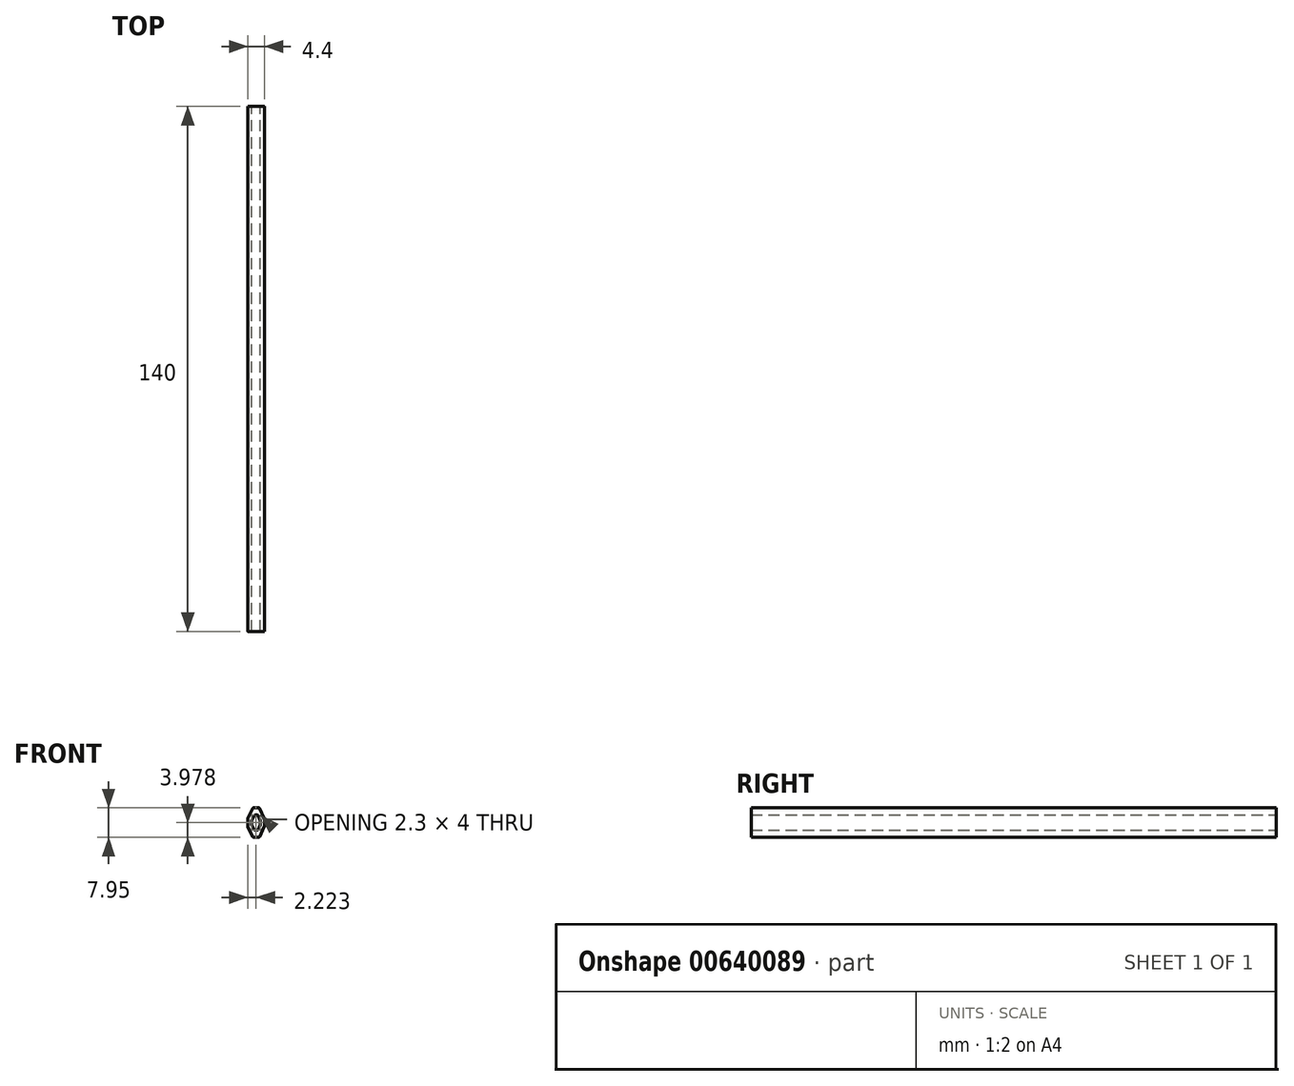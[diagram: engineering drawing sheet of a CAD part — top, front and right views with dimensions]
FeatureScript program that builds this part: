
annotation { "Feature Type Name" : "Feature", "Feature Type Description" : "" }
export const myFeature = defineFeature(function(context is Context, id is Id, definition is map)
    precondition{}
    {
        {
            var Q0;
            Q0=qCreatedBy(makeId("Front.planeOp"),FACE);
            var sketch = newSketch(context, id + "F0", { "sketchPlane" : qUnion([Q0])});
            skLineSegment(sketch, "E0", {"start": v(0, 5.06) * mm, "end": v(0, 2.96) * mm});
            skLineSegment(sketch, "E1", {"start": v(0, 2.96) * mm, "end": v(1.41, 0) * mm});
            skLineSegment(sketch, "E2", {"start": v(1.41, 0) * mm, "end": v(3.03, 0) * mm});
            skLineSegment(sketch, "E3", {"start": v(3.03, 0) * mm, "end": v(4.4, 2.87) * mm});
            skLineSegment(sketch, "E4", {"start": v(4.4, 2.87) * mm, "end": v(4.4, 5.06) * mm});
            skLineSegment(sketch, "E5", {"start": v(4.4, 5.06) * mm, "end": v(3.05, 7.95) * mm});
            skLineSegment(sketch, "E6", {"start": v(3.05, 7.95) * mm, "end": v(1.41, 7.95) * mm});
            skLineSegment(sketch, "E7", {"start": v(1.41, 7.95) * mm, "end": v(0, 5.06) * mm});
            skLineSegment(sketch, "E8", {"start": v(1.07, 4.51) * mm, "end": v(1.07, 3.41) * mm});
            skLineSegment(sketch, "E9", {"start": v(1.07, 3.41) * mm, "end": v(1.76, 1.98) * mm});
            skLineSegment(sketch, "E10", {"start": v(1.76, 1.98) * mm, "end": v(2.69, 1.98) * mm});
            skLineSegment(sketch, "E11", {"start": v(2.69, 1.98) * mm, "end": v(3.37, 3.41) * mm});
            skLineSegment(sketch, "E12", {"start": v(3.37, 3.41) * mm, "end": v(3.37, 4.51) * mm});
            skLineSegment(sketch, "E13", {"start": v(3.37, 4.51) * mm, "end": v(2.69, 5.98) * mm});
            skLineSegment(sketch, "E14", {"start": v(2.69, 5.98) * mm, "end": v(1.79, 5.98) * mm});
            skLineSegment(sketch, "E15", {"start": v(1.79, 5.98) * mm, "end": v(1.07, 4.51) * mm});
            skLineSegment(sketch, "E16", {"start": v(3.37, 4.51) * mm, "end": v(4.4, 5.06) * mm, "construction": true});
            skLineSegment(sketch, "E17", {"start": v(3.37, 3.41) * mm, "end": v(4.4, 2.87) * mm, "construction": true});
            skLineSegment(sketch, "E18", {"start": v(1.07, 3.41) * mm, "end": v(0, 2.96) * mm, "construction": true});
            skLineSegment(sketch, "E19", {"start": v(2.69, 1.98) * mm, "end": v(3.03, 0) * mm, "construction": true});
            skLineSegment(sketch, "E20", {"start": v(1.76, 1.98) * mm, "end": v(1.41, 0) * mm, "construction": true});
            skLineSegment(sketch, "E21", {"start": v(1.41, 7.95) * mm, "end": v(1.79, 5.98) * mm, "construction": true});
            skLineSegment(sketch, "E22", {"start": v(0, 5.06) * mm, "end": v(4.4, 5.06) * mm, "construction": true});
            skLineSegment(sketch, "E23", {"start": v(1.41, 0) * mm, "end": v(1.41, 7.95) * mm, "construction": true});
            skLineSegment(sketch, "E24", {"start": v(1.07, 3.41) * mm, "end": v(3.37, 3.41) * mm, "construction": true});
            skSolve(sketch);
        }
        {
            var Q0;
            Q0=makeQuery(id+"F0.imprint","IMPRINT",FACE,{"disambiguationData":[TD([[makeQuery(id+"F0.imprint","IMPRINT",EDGE,{"derivedFrom":sQuery(id+"F0.wireOp",EDGE,"E0")}),1.0]])]});
            extrude(context, id + "F1", {"entities" : qUnion([Q0]), "depth" : 140 * mm, "offsetDistance" : 25 * mm});
        }
        {
            var Q0;
            Q0=makeQuery(id+"F1.opExtrude","SWEPT_EDGE",EDGE,{"disambiguationData":[OSD([sQuery(id+"F0.wireOp",EDGE,"E5"),sQuery(id+"F0.wireOp",EDGE,"E6")])]});
            var Q1;
            Q1=makeQuery(id+"F1.opExtrude","SWEPT_EDGE",EDGE,{"disambiguationData":[OSD([sQuery(id+"F0.wireOp",EDGE,"E6"),sQuery(id+"F0.wireOp",EDGE,"E7")])]});
            var Q2;
            Q2=makeQuery(id+"F1.opExtrude","SWEPT_EDGE",EDGE,{"disambiguationData":[OSD([sQuery(id+"F0.wireOp",EDGE,"E2"),sQuery(id+"F0.wireOp",EDGE,"E3")])]});
            var Q3;
            Q3=makeQuery(id+"F1.opExtrude","SWEPT_EDGE",EDGE,{"disambiguationData":[OSD([sQuery(id+"F0.wireOp",EDGE,"E1"),sQuery(id+"F0.wireOp",EDGE,"E2")])]});
            fillet(context, id + "F2", {"entities" : qUnion([Q0, Q1, Q2, Q3]), "radius" : 0.4 * mm, "tangentPropagation" : true, "allowEdgeOverflow" : false});
        }
        {
            var Q0;
            Q0=makeQuery(id+"F1.opExtrude","SWEPT_EDGE",EDGE,{"disambiguationData":[OSD([sQuery(id+"F0.wireOp",EDGE,"E4"),sQuery(id+"F0.wireOp",EDGE,"E5")])]});
            var Q1;
            Q1=makeQuery(id+"F1.opExtrude","SWEPT_EDGE",EDGE,{"disambiguationData":[OSD([sQuery(id+"F0.wireOp",EDGE,"E3"),sQuery(id+"F0.wireOp",EDGE,"E4")])]});
            var Q2;
            Q2=makeQuery(id+"F1.opExtrude","SWEPT_EDGE",EDGE,{"disambiguationData":[OSD([sQuery(id+"F0.wireOp",EDGE,"E0"),sQuery(id+"F0.wireOp",EDGE,"E7")])]});
            var Q3;
            Q3=makeQuery(id+"F1.opExtrude","SWEPT_EDGE",EDGE,{"disambiguationData":[OSD([sQuery(id+"F0.wireOp",EDGE,"E0"),sQuery(id+"F0.wireOp",EDGE,"E1")])]});
            var Q4;
            Q4=makeQuery(id+"F1.opExtrude","SWEPT_EDGE",EDGE,{"disambiguationData":[OSD([sQuery(id+"F0.wireOp",EDGE,"E9"),sQuery(id+"F0.wireOp",EDGE,"E10")])]});
            var Q5;
            Q5=makeQuery(id+"F1.opExtrude","SWEPT_EDGE",EDGE,{"disambiguationData":[OSD([sQuery(id+"F0.wireOp",EDGE,"E14"),sQuery(id+"F0.wireOp",EDGE,"E15")])]});
            var Q6;
            Q6=makeQuery(id+"F1.opExtrude","SWEPT_EDGE",EDGE,{"disambiguationData":[OSD([sQuery(id+"F0.wireOp",EDGE,"E13"),sQuery(id+"F0.wireOp",EDGE,"E14")])]});
            var Q7;
            Q7=makeQuery(id+"F1.opExtrude","SWEPT_EDGE",EDGE,{"disambiguationData":[OSD([sQuery(id+"F0.wireOp",EDGE,"E10"),sQuery(id+"F0.wireOp",EDGE,"E11")])]});
            fillet(context, id + "F3", {"entities" : qUnion([Q0, Q1, Q2, Q3, Q4, Q5, Q6, Q7]), "radius" : 0.25 * mm, "tangentPropagation" : true, "allowEdgeOverflow" : false});
        }
        {
            var Q0;
            Q0=makeQuery(id+"F1.opExtrude","SWEPT_EDGE",EDGE,{"disambiguationData":[OSD([sQuery(id+"F0.wireOp",EDGE,"E8"),sQuery(id+"F0.wireOp",EDGE,"E15")])]});
            var Q1;
            Q1=makeQuery(id+"F1.opExtrude","SWEPT_EDGE",EDGE,{"disambiguationData":[OSD([sQuery(id+"F0.wireOp",EDGE,"E8"),sQuery(id+"F0.wireOp",EDGE,"E9")])]});
            var Q2;
            Q2=makeQuery(id+"F1.opExtrude","SWEPT_EDGE",EDGE,{"disambiguationData":[OSD([sQuery(id+"F0.wireOp",EDGE,"E12"),sQuery(id+"F0.wireOp",EDGE,"E13")])]});
            var Q3;
            Q3=makeQuery(id+"F1.opExtrude","SWEPT_EDGE",EDGE,{"disambiguationData":[OSD([sQuery(id+"F0.wireOp",EDGE,"E11"),sQuery(id+"F0.wireOp",EDGE,"E12")])]});
            fillet(context, id + "F4", {"entities" : qUnion([Q0, Q1, Q2, Q3]), "radius" : .15 * mm, "tangentPropagation" : true, "allowEdgeOverflow" : false});
        }
    });
